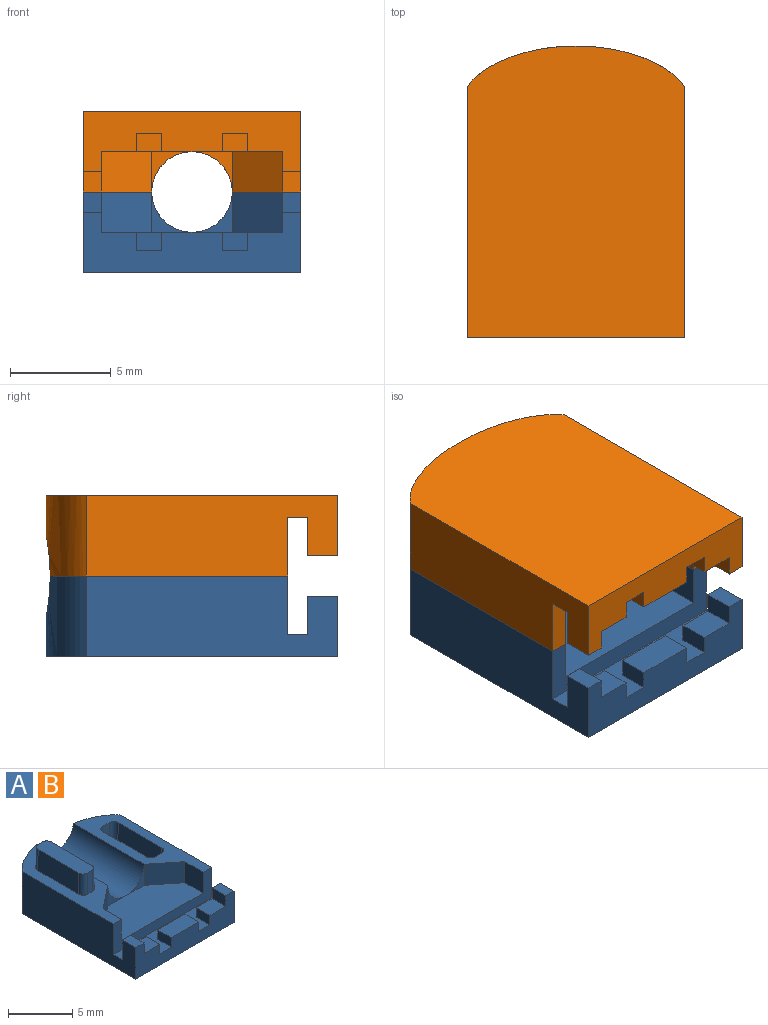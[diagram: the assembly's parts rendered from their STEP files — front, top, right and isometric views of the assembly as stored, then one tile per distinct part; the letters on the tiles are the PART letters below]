
ASSEMBLY  parts=2 mates=1
PART A: 49 faces, bbox 10.8x14.6x6 mm
  f0: plane 11.88x3.47mm, normal (0,0,1), area 22.4mm2, adj f9,f10,f16,f18,f21,f28,f29,f30
  f1: plane 2x2mm, normal (0,-1,0), area 0.9mm2, adj f12,f19,f48
  f2: plane 1.5x1mm, normal (1,0,0), area 1.5mm2, adj f5,f8,f13,f47
  f3: plane 1.5x1mm, normal (-1,0,0), area 1.5mm2, adj f6,f8,f15,f46
  f4: plane 12.5x4mm, normal (1,0,0), area 45.6mm2, adj f6,f7,f8,f16,f17,f21,f27,f46
  f5: plane 2.65x1.9mm, normal (0,1,0), area 3.3mm2, adj f2,f9,f13,f22,f27,f47
  f6: plane 2.65x1.9mm, normal (0,1,0), area 3.3mm2, adj f3,f4,f15,f26,f27,f46
  f7: plane 11.88x3.47mm, normal (0,0,1), area 20.8mm2, adj f4,f11,f16,f19,f21,f37,f38,f39
  f8: plane 10.8x3mm, normal (0,-1,0), area 21.1mm2, adj f2,f3,f4,f9,f13,f14,f15,f17
  f9: plane 12.5x4mm, normal (-1,0,0), area 45.6mm2, adj f0,f5,f8,f16,f17,f21,f27,f47
  f10: plane 2x2mm, normal (1,0,0), area 4mm2, adj f0,f12,f18,f21
  f11: plane 2x2mm, normal (-1,0,0), area 4mm2, adj f7,f12,f19,f21
  f12: plane 9x4mm, normal (0,0,1), area 31mm2, adj f1,f10,f11,f18,f19,f20,f21
  f13: plane 1.75x1.5mm, normal (0,0,1), area 2.6mm2, adj f2,f5,f8,f22
  f14: plane 3x1.5mm, normal (0,0,1), area 4.5mm2, adj f8,f23,f24,f25
  f15: plane 1.75x1.5mm, normal (0,0,1), area 2.6mm2, adj f3,f6,f8,f26
  f16: extruded ~10.8x4mm, area 41.2mm2, adj f0,f4,f7,f9,f17,f48
  f17: plane 14.65x10.8mm, normal (0,0,-1), area 150.6mm2, adj f4,f8,f9,f16
  f18: plane 2.5x2mm, normal (0.62,-0.78,0), area 6.4mm2, adj f0,f10,f12,f20
  f19: plane 2.5x2mm, normal (-0.62,-0.78,0), area 6.4mm2, adj f1,f7,f11,f12
  f20: plane 2x2mm, normal (0,-1,0), area 0.9mm2, adj f12,f18,f48
  f21: plane 10.8x2.9mm, normal (0,-1,0), area 13.3mm2, adj f0,f4,f7,f9,f10,f11,f12,f27
  f22: plane 1.5x0.9mm, normal (1,0,0), area 1.3mm2, adj f5,f8,f13,f27
  f23: plane 1.5x0.9mm, normal (-1,0,0), area 1.3mm2, adj f8,f14,f24,f27
  f24: plane 3x0.9mm, normal (0,1,0), area 2.7mm2, adj f14,f23,f25,f27
  f25: plane 1.5x0.9mm, normal (1,0,0), area 1.3mm2, adj f8,f14,f24,f27
  f26: plane 1.5x0.9mm, normal (-1,0,0), area 1.3mm2, adj f6,f8,f15,f27
  f27: plane 10.8x2.5mm, normal (0,0,1), area 14.5mm2, adj f4,f5,f6,f8,f9,f21,f22,f23
  f28: plane 4.5x2mm, normal (1,0,0.02), area 9mm2, adj f0,f29,f35,f36
  f29: cone r=0.5mm half-angle=1deg, axis (0,0,-1), area 1.5mm2, adj f0,f28,f30,f36
  f30: plane 2x0.5mm, normal (0,1,0.02), area 1mm2, adj f0,f29,f31,f36
  f31: cone r=0.5mm half-angle=1deg, axis (0,0,-1), area 1.5mm2, adj f0,f30,f32,f36
  f32: plane 4.5x2mm, normal (-1,0,0.02), area 9mm2, adj f0,f31,f33,f36
  f33: cone r=0.5mm half-angle=1deg, axis (0,0,-1), area 1.5mm2, adj f0,f32,f34,f36
  f34: plane 2x0.5mm, normal (0,-1,0.02), area 1mm2, adj f0,f33,f35,f36
  f35: cone r=0.5mm half-angle=1deg, axis (0,0,-1), area 1.5mm2, adj f0,f28,f34,f36
  f36: plane 5.43x1.43mm, normal (0,0,1), area 7.6mm2, adj f28,f29,f30,f31,f32,f33,f34,f35
  f37: plane 4.8x2mm, normal (-1,0,0.02), area 9.6mm2, adj f7,f38,f44,f45
  f38: cone r=0.5mm half-angle=1deg, axis (0,0,1), area 1.5mm2, adj f7,f37,f39,f45
  f39: plane 2x0.7mm, normal (0,-1,0.02), area 1.4mm2, adj f7,f38,f40,f45
  f40: cone r=0.5mm half-angle=1deg, axis (0,0,1), area 1.5mm2, adj f7,f39,f41,f45
  f41: plane 4.8x2mm, normal (1,0,0.02), area 9.6mm2, adj f7,f40,f42,f45
  f42: cone r=0.5mm half-angle=1deg, axis (0,0,1), area 1.5mm2, adj f7,f41,f43,f45
  f43: plane 2x0.7mm, normal (0,1,0.02), area 1.4mm2, adj f7,f42,f44,f45
  f44: cone r=0.5mm half-angle=1deg, axis (0,0,1), area 1.5mm2, adj f7,f37,f43,f45
  f45: plane 5.73x1.63mm, normal (0,0,1), area 9.2mm2, adj f37,f38,f39,f40,f41,f42,f43,f44
  f46: plane 1.5x0.9mm, normal (0,0,1), area 1.4mm2, adj f3,f4,f6,f8
  f47: plane 1.5x0.9mm, normal (0,0,1), area 1.3mm2, adj f2,f5,f8,f9
  f48: cylinder r=2mm len=8mm, axis (0,-1,0), area 49.7mm2, adj f0,f1,f7,f16,f20
PART B: same geometry as A
PLACE A t=(10.49,9.96,7.97)mm
PLACE B rot(axis=(0,1,0),180deg) t=(10.49,9.96,7.97)mm
MATE fastened B.f0 <-> A.f0  axis (0,0,-1) through (10.49,9.96,7.97)mm
